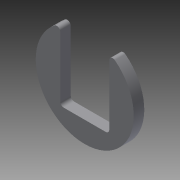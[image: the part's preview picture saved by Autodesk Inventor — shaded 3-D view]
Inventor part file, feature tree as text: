
AUTODESK INVENTOR PART (.ipt)
format: ipt  version: 2015 (Build 190159000, 159)  size: 88,064 bytes
history: native  units: mm
features: extrude x1, sketch x1
ambient origin geometry x8: Origin, YZ Plane, XZ Plane, XY Plane, X Axis, Y Axis, Z Axis, Center Point
bodies: Solid1 (feature_tree)
feature tree (2):
  extrude  "Extrusion1"  Depth=14.0mm
  sketch  "Sketch1"  dims[d0=28.0mm d2=14.0mm d4=1.0mm d5=8.0mm d6=3.0mm d7=0.0mm]
